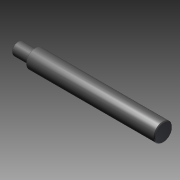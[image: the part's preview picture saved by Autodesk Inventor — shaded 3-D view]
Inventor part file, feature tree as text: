
AUTODESK INVENTOR PART (.ipt)
format: ipt  version: 2011 SP1 (Build 150282100, 282)  size: 92,160 bytes
history: native  units: mm
features: revolve x1, sketch x1
ambient origin geometry x8: Origin, YZ Plane, XZ Plane, XY Plane, X Axis, Y Axis, Z Axis, Center Point
bodies: Solid1 (feature_tree)
feature tree (2):
  revolve  "Revolution1"  [1 undecoded]
  sketch  "Sketch_1"  dims[d0=360.0deg]
note: 1 required parameter value undecoded (feature->parameter linkage not recoverable at this tier; creation-order binding heuristic only, values carry confidence <= 0.55)
